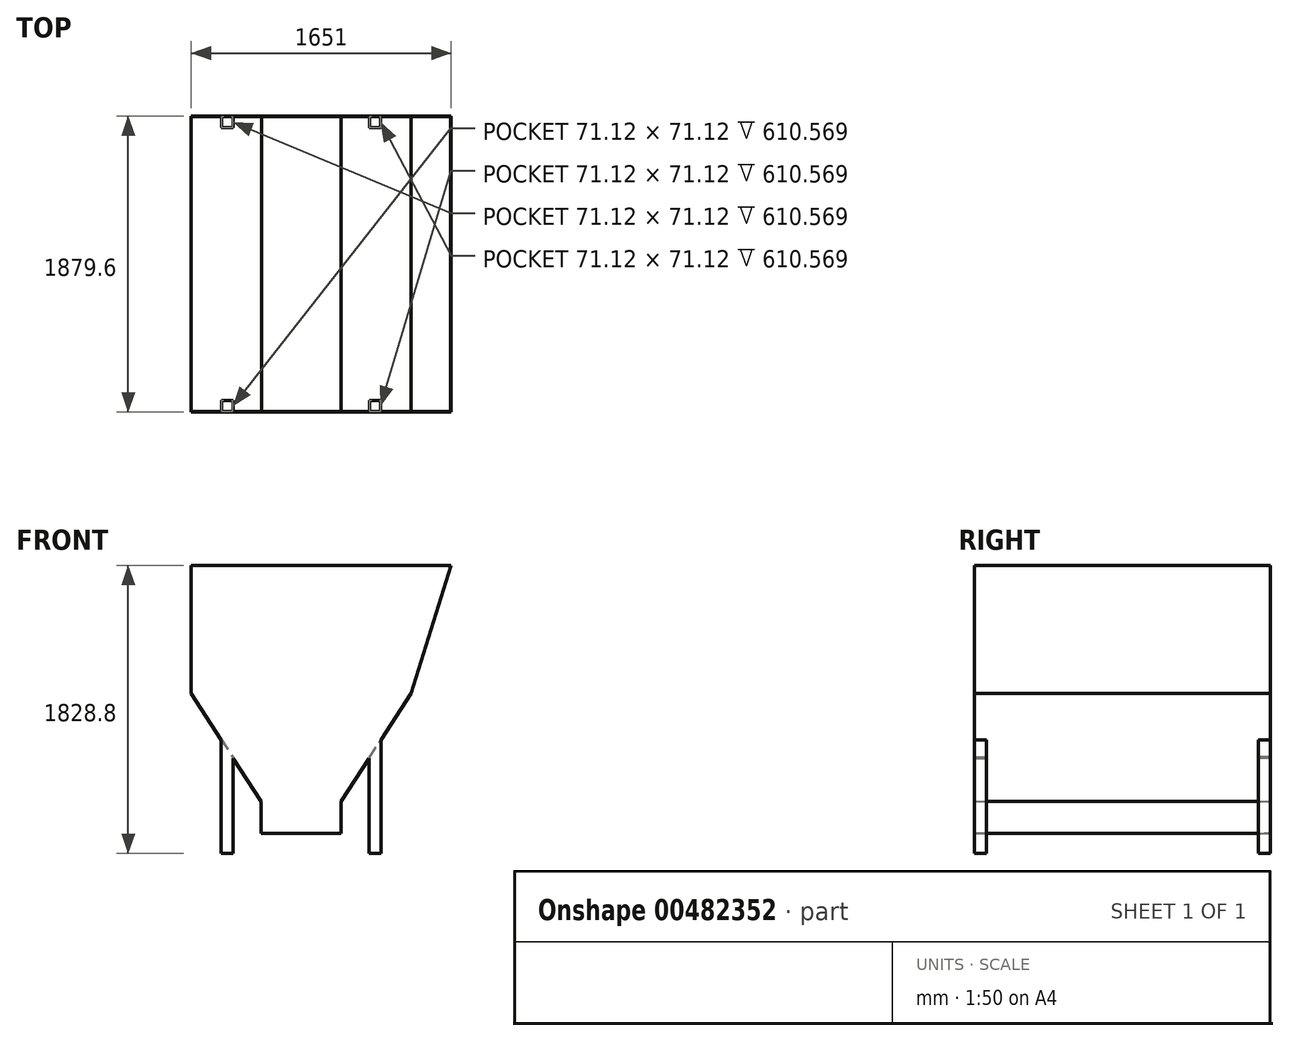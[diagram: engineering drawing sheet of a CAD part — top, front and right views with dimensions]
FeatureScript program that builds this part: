
annotation { "Feature Type Name" : "Feature", "Feature Type Description" : "" }
export const myFeature = defineFeature(function(context is Context, id is Id, definition is map)
    precondition{}
    {
        {
            var Q0;
            Q0=qCreatedBy(makeId("Front.planeOp"),FACE);
            var sketch = newSketch(context, id + "F0", { "sketchPlane" : qUnion([Q0])});
            skLineSegment(sketch, "E0", {"start": v(0, 127) * mm, "end": v(-254, 127) * mm});
            skLineSegment(sketch, "E1", {"start": v(-254, 127) * mm, "end": v(-254, 330.2) * mm});
            skLineSegment(sketch, "E2", {"start": v(-254, 330.2) * mm, "end": v(-698.5, 1016) * mm});
            skLineSegment(sketch, "E3", {"start": v(-698.5, 1828.8) * mm, "end": v(0, 1828.8) * mm});
            skLineSegment(sketch, "E4", {"start": v(0, 212.3) * mm, "end": v(0, 127) * mm, "construction": true});
            skLineSegment(sketch, "E5.MirrorCS", {"start": v(0, 127) * mm, "end": v(254, 127) * mm});
            skLineSegment(sketch, "E6.MirrorCS", {"start": v(254, 127) * mm, "end": v(254, 330.2) * mm});
            skLineSegment(sketch, "E7.MirrorCS", {"start": v(698.5, 1016) * mm, "end": v(952.5, 1828.8) * mm});
            skLineSegment(sketch, "E8.MirrorCS", {"start": v(952.5, 1828.8) * mm, "end": v(0, 1828.8) * mm});
            skLineSegment(sketch, "E9.MirrorCS", {"start": v(254, 330.2) * mm, "end": v(698.5, 1016) * mm});
            skPoint(sketch, "E10", {"position": v(-583.26, 838.2) * mm});
            skLineSegment(sketch, "E11", {"start": v(-698.5, 1016) * mm, "end": v(-698.5, 1828.8) * mm});
            skSolve(sketch);
        }
        {
            var Q0;
            Q0 = qSketchRegion(id + "F0", true);
            extrude(context, id + "F1", {"entities" : qUnion([Q0]), "depth" : 1879.6 * mm, "offsetDistance" : 25.4 * mm});
        }
        {
            var Q0;
            Q0=qCreatedBy(makeId("Top.planeOp"),FACE);
            var sketch = newSketch(context, id + "F2", { "sketchPlane" : qUnion([Q0])});
            skLineSegment(sketch, "E12.bottom", {"start": v(-431.8, -1803.4) * mm, "end": v(-508, -1803.4) * mm});
            skLineSegment(sketch, "E12.top", {"start": v(-431.8, -1879.6) * mm, "end": v(-508, -1879.6) * mm});
            skLineSegment(sketch, "E12.left", {"start": v(-431.8, -1803.4) * mm, "end": v(-431.8, -1879.6) * mm});
            skLineSegment(sketch, "E12.right", {"start": v(-508, -1803.4) * mm, "end": v(-508, -1879.6) * mm});
            skLineSegment(sketch, "E13", {"start": v(0, 0) * mm, "end": v(0, -538.07) * mm, "construction": true});
            skLineSegment(sketch, "E14.MirrorCS", {"start": v(508, -1803.4) * mm, "end": v(508, -1879.6) * mm});
            skLineSegment(sketch, "E15.MirrorCS", {"start": v(431.8, -1803.4) * mm, "end": v(431.8, -1879.6) * mm});
            skLineSegment(sketch, "E16.MirrorCS", {"start": v(431.8, -1803.4) * mm, "end": v(508, -1803.4) * mm});
            skLineSegment(sketch, "E17.MirrorCS", {"start": v(431.8, -1879.6) * mm, "end": v(508, -1879.6) * mm});
            skLineSegment(sketch, "E18", {"start": v(-698.5, -939.8) * mm, "end": v(-1194.6, -939.8) * mm, "construction": true});
            skLineSegment(sketch, "E19.MirrorCS", {"start": v(-431.8, 0) * mm, "end": v(-508, 0) * mm});
            skLineSegment(sketch, "E20.MirrorCS", {"start": v(431.8, 0) * mm, "end": v(508, 0) * mm});
            skLineSegment(sketch, "E21.MirrorCS", {"start": v(431.8, -76.2) * mm, "end": v(431.8, 0) * mm});
            skLineSegment(sketch, "E22.MirrorCS", {"start": v(431.8, -76.2) * mm, "end": v(508, -76.2) * mm});
            skLineSegment(sketch, "E23.MirrorCS", {"start": v(-431.8, -76.2) * mm, "end": v(-431.8, 0) * mm});
            skLineSegment(sketch, "E24.MirrorCS", {"start": v(508, -76.2) * mm, "end": v(508, 0) * mm});
            skLineSegment(sketch, "E25.MirrorCS", {"start": v(-508, -76.2) * mm, "end": v(-508, 0) * mm});
            skLineSegment(sketch, "E26.MirrorCS", {"start": v(-431.8, -76.2) * mm, "end": v(-508, -76.2) * mm});
            skSolve(sketch);
        }
        {
            var Q0;
            Q0 = qSketchRegion(id + "F2", true);
            extrude(context, id + "F3", {"entities" : qUnion([Q0]), "operationType" : NewBodyOperationType.ADD, "endBound" : BoundingType.UP_TO_NEXT, "depth" : 25.4 * mm, "offsetDistance" : 25.4 * mm});
        }
        {
            var Q0;
            Q0=makeQuery(id+"F1.opExtrude","SWEPT_FACE",FACE,{"disambiguationData":[OSD([sQuery(id+"F0.wireOp",EDGE,"E3"),sQuery(id+"F0.wireOp",EDGE,"E8.MirrorCS")])]});
            var Q1;
            Q1=makeQuery(id+"F1.opExtrude","SWEPT_FACE",FACE,{"disambiguationData":[OSD([sQuery(id+"F0.wireOp",EDGE,"E11")])]});
            shell(context, id + "F4", {"entities" : qUnion([Q0, Q1]), "thickness" : 2.54 * mm});
        }
    });
